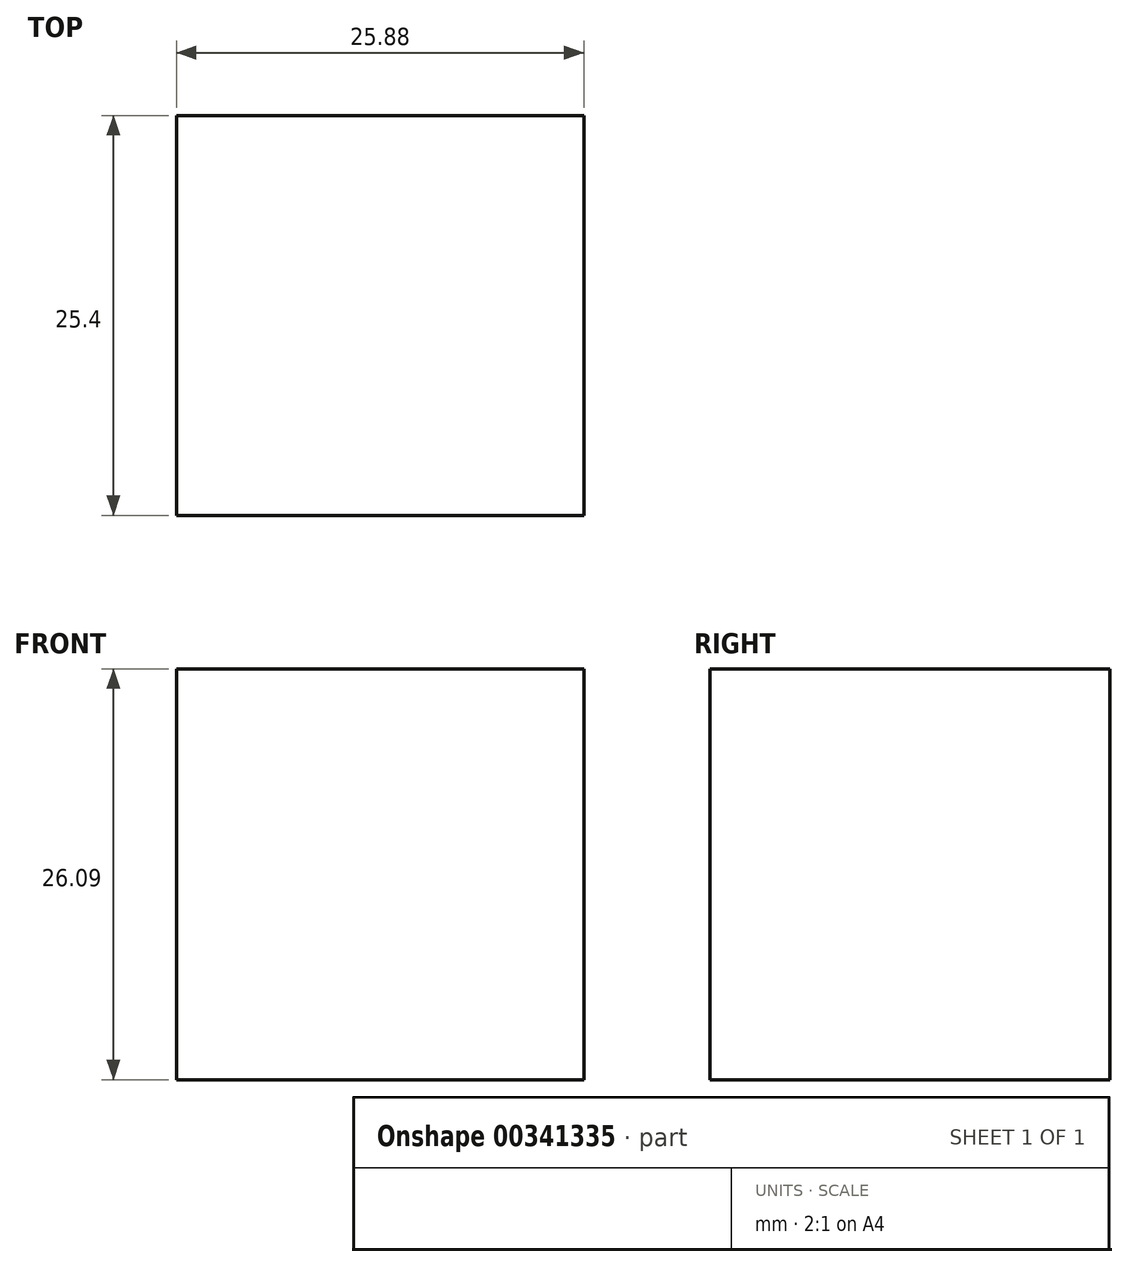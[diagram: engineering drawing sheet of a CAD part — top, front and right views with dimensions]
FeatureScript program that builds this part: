
annotation { "Feature Type Name" : "Feature", "Feature Type Description" : "" }
export const myFeature = defineFeature(function(context is Context, id is Id, definition is map)
    precondition{}
    {
        {
            var Q0;
            Q0=qCreatedBy(makeId("Front.planeOp"),FACE);
            var sketch = newSketch(context, id + "F0", { "sketchPlane" : qUnion([Q0])});
            skLineSegment(sketch, "E0.bottom", {"start": v(-12.22, -34.4) * mm, "end": v(13.66, -34.4) * mm});
            skLineSegment(sketch, "E0.top", {"start": v(-12.22, -60.5) * mm, "end": v(13.66, -60.5) * mm});
            skLineSegment(sketch, "E0.left", {"start": v(-12.22, -34.4) * mm, "end": v(-12.22, -60.5) * mm});
            skLineSegment(sketch, "E0.right", {"start": v(13.66, -34.4) * mm, "end": v(13.66, -60.5) * mm});
            skLineSegment(sketch, "E1.bottom", {"start": v(-5.03, -2.16) * mm, "end": v(5.44, -2.16) * mm});
            skLineSegment(sketch, "E1.top", {"start": v(-5.03, -34.4) * mm, "end": v(5.44, -34.4) * mm});
            skLineSegment(sketch, "E1.left", {"start": v(-5.03, -2.16) * mm, "end": v(-5.03, -34.4) * mm});
            skLineSegment(sketch, "E1.right", {"start": v(5.44, -2.16) * mm, "end": v(5.44, -34.4) * mm});
            skCircle(sketch, "E2", {"center": v(0, -2.16) * mm, "radius": 5.52 * mm});
            skLineSegment(sketch, "E3", {"start": v(-3.36, 2.22) * mm, "end": v(26.9, 38.11) * mm});
            skLineSegment(sketch, "E4", {"start": v(26.9, 38.11) * mm, "end": v(33.84, 32.27) * mm});
            skLineSegment(sketch, "E5", {"start": v(33.84, 32.27) * mm, "end": v(5.44, -2.16) * mm});
            skCircle(sketch, "E6", {"center": v(30.37, 35.2) * mm, "radius": 5.2 * mm});
            skLineSegment(sketch, "E7.bottom", {"start": v(30.8, 40.37) * mm, "end": v(48.66, 40.37) * mm});
            skLineSegment(sketch, "E7.top", {"start": v(30.8, 40.2) * mm, "end": v(48.66, 40.2) * mm});
            skLineSegment(sketch, "E7.left", {"start": v(30.8, 40.37) * mm, "end": v(30.8, 40.2) * mm});
            skLineSegment(sketch, "E7.right", {"start": v(48.66, 40.37) * mm, "end": v(48.66, 40.2) * mm});
            skLineSegment(sketch, "E8", {"start": v(48.66, 40.37) * mm, "end": v(48.66, 31.87) * mm});
            skLineSegment(sketch, "E9", {"start": v(48.66, 31.87) * mm, "end": v(33.84, 32.27) * mm});
            skSolve(sketch);
        }
        {
            var Q0;
            Q0=makeQuery(id+"F0.imprint","IMPRINT",FACE,{"disambiguationData":[TD([[makeQuery(id+"F0.imprint","IMPRINT",EDGE,{"derivedFrom":sQuery(id+"F0.wireOp",EDGE,"E0.top")}),1.0]])]});
            extrude(context, id + "F1", {"entities" : qUnion([Q0]), "endBound" : BoundingType.SYMMETRIC, "depth" : 25.4 * mm});
        }
    });
